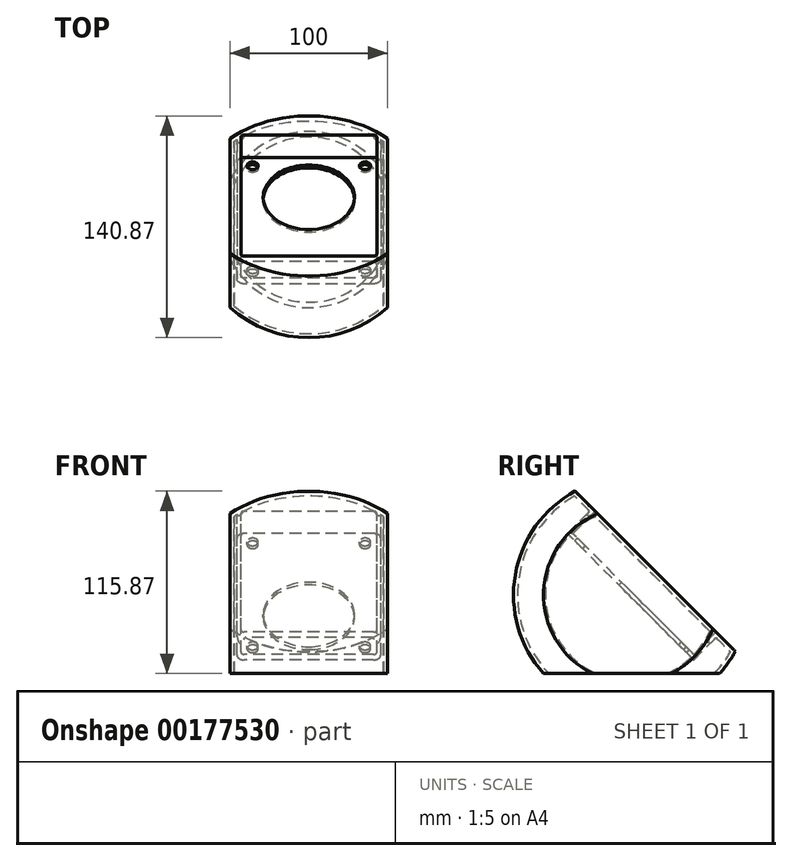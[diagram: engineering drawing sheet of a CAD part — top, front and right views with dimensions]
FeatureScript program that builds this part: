
annotation { "Feature Type Name" : "Feature", "Feature Type Description" : "" }
export const myFeature = defineFeature(function(context is Context, id is Id, definition is map)
    precondition{}
    {
        {
            var Q0;
            Q0=qCreatedBy(makeId("Front.planeOp"),FACE);
            var sketch = newSketch(context, id + "F0", { "sketchPlane" : qUnion([Q0])});
            skArc(sketch, "E0", {"start": v(55.9, 0) * mm, "mid": v(68.47, 80.62) * mm, "end": v(0, 125) * mm});
            skLineSegment(sketch, "E1", {"start": v(0, 0) * mm, "end": v(55.9, 0) * mm});
            skLineSegment(sketch, "E2", {"start": v(0, 50) * mm, "end": v(0, 0) * mm, "construction": true});
            skLineSegment(sketch, "E3", {"start": v(0, 0) * mm, "end": v(0, 125) * mm});
            skPoint(sketch, "E4.orphan", {"position": v(-55.9, 0) * mm});
            skSolve(sketch);
        }
        {
            var Q0;
            Q0=makeQuery(id+"F0.imprint","IMPRINT",FACE,{"disambiguationData":[TD([[makeQuery(id+"F0.imprint","IMPRINT",EDGE,{"derivedFrom":sQuery(id+"F0.wireOp",EDGE,"E0")}),1.0]])]});
            var Q1;
            Q1=sQuery(id+"F0.wireOp",EDGE,"E2");
            revolve(context, id + "F1", {"entities" : qUnion([Q0]), "axis" : qUnion([Q1]), "revolveType" : RevolveType.FULL});
        }
        {
            var Q0;
            Q0=makeQuery(id+"F1.opRevolve","SWEPT_FACE",FACE,{"disambiguationData":[OSD([sQuery(id+"F0.wireOp",EDGE,"E1")])]});
            var sketch = newSketch(context, id + "F2", { "sketchPlane" : qUnion([Q0])});
            skLineSegment(sketch, "E5", {"start": v(74.71, -80) * mm, "end": v(-64.99, -80) * mm, "construction": true});
            skSolve(sketch);
        }
        {
            var Q0;
            Q0=sQuery(id+"F2.wireOp",EDGE,"E5");
            cPlane(context, id + "F3", {"entities" : qUnion([Q0]), "cplaneType" : CPlaneType.LINE_ANGLE, "offset" : 25 * mm, "angle" : 45 * degree, "oppositeDirection" : true, "width" : 150 * mm, "height" : 150 * mm});
        }
        {
            var Q0;
            Q0=qCreatedBy(id+"F3.planeOp",FACE);
            var sketch = newSketch(context, id + "F4", { "sketchPlane" : qUnion([Q0])});
            skLineSegment(sketch, "E6.bottom", {"start": v(-80.9, 121.62) * mm, "end": v(80.9, 121.62) * mm});
            skLineSegment(sketch, "E6.top", {"start": v(-80.9, -121.62) * mm, "end": v(80.9, -121.62) * mm});
            skLineSegment(sketch, "E6.left", {"start": v(-80.9, 121.62) * mm, "end": v(-80.9, -121.62) * mm});
            skLineSegment(sketch, "E6.right", {"start": v(80.9, 121.62) * mm, "end": v(80.9, -121.62) * mm});
            skPoint(sketch, "E6.middle", {"position": v(0, 0) * mm});
            skSolve(sketch);
        }
        {
            var Q0;
            Q0=makeQuery(id+"F4.imprint","IMPRINT",FACE,{"disambiguationData":[TD([[makeQuery(id+"F4.imprint","IMPRINT",EDGE,{"derivedFrom":sQuery(id+"F4.wireOp",EDGE,"E6.bottom")}),-1.0]])]});
            extrude(context, id + "F5", {"entities" : qUnion([Q0]), "operationType" : NewBodyOperationType.REMOVE, "oppositeDirection" : true, "depth" : 100 * mm});
        }
        {
            var Q0;
            Q0=qCreatedBy(id+"F3.planeOp",FACE);
            var sketch = newSketch(context, id + "F6", { "sketchPlane" : qUnion([Q0])});
            skLineSegment(sketch, "E7.bottom", {"start": v(43.2, -17.25) * mm, "end": v(43.2, 87.25) * mm});
            skLineSegment(sketch, "E7.top", {"start": v(-43.2, -17.25) * mm, "end": v(-43.2, 87.25) * mm});
            skLineSegment(sketch, "E7.left", {"start": v(41.2, -19.25) * mm, "end": v(-41.2, -19.25) * mm});
            skLineSegment(sketch, "E7.right", {"start": v(41.2, 89.25) * mm, "end": v(-41.2, 89.25) * mm});
            skPoint(sketch, "E7.middle", {"position": v(0, 35) * mm});
            skPoint(sketch, "E8.visualSharp", {"position": v(-43.2, 89.25) * mm});
            skArc(sketch, "E8.filletArc", {"start": v(-41.2, 89.25) * mm, "mid": v(-42.61, 88.66) * mm, "end": v(-43.2, 87.25) * mm});
            skPoint(sketch, "E9.visualSharp", {"position": v(43.2, 89.25) * mm});
            skArc(sketch, "E9.filletArc", {"start": v(43.2, 87.25) * mm, "mid": v(42.61, 88.66) * mm, "end": v(41.2, 89.25) * mm});
            skPoint(sketch, "E10.visualSharp", {"position": v(43.2, -19.25) * mm});
            skArc(sketch, "E10.filletArc", {"start": v(41.2, -19.25) * mm, "mid": v(42.61, -18.66) * mm, "end": v(43.2, -17.25) * mm});
            skPoint(sketch, "E11.visualSharp", {"position": v(-43.2, -19.25) * mm});
            skArc(sketch, "E11.filletArc", {"start": v(-43.2, -17.25) * mm, "mid": v(-42.61, -18.66) * mm, "end": v(-41.2, -19.25) * mm});
            skCircle(sketch, "E12", {"center": v(0, 16.55) * mm, "radius": 29 * mm});
            skCircle(sketch, "E13", {"center": v(-35.7, 81.75) * mm, "radius": 3.5 * mm});
            skCircle(sketch, "E14", {"center": v(35.7, 81.75) * mm, "radius": 3.5 * mm});
            skCircle(sketch, "E15", {"center": v(35.7, -11.75) * mm, "radius": 3.5 * mm});
            skCircle(sketch, "E16", {"center": v(-35.7, -11.75) * mm, "radius": 3.5 * mm});
            skSolve(sketch);
        }
        {
            var Q0;
            Q0=makeQuery(id+"F6.imprint","IMPRINT",FACE,{"disambiguationData":[TD([[makeQuery(id+"F6.imprint","IMPRINT",EDGE,{"derivedFrom":sQuery(id+"F6.wireOp",EDGE,"E12")}),1.0]])]});
            var Q1;
            Q1=makeQuery(id+"F6.imprint","IMPRINT",FACE,{"disambiguationData":[TD([[makeQuery(id+"F6.imprint","IMPRINT",EDGE,{"derivedFrom":sQuery(id+"F6.wireOp",EDGE,"E13")}),1.0]])]});
            var Q2;
            Q2=makeQuery(id+"F6.imprint","IMPRINT",FACE,{"disambiguationData":[TD([[makeQuery(id+"F6.imprint","IMPRINT",EDGE,{"derivedFrom":sQuery(id+"F6.wireOp",EDGE,"E7.bottom")}),1.0]])]});
            var Q3;
            Q3=makeQuery(id+"F6.imprint","IMPRINT",FACE,{"disambiguationData":[TD([[makeQuery(id+"F6.imprint","IMPRINT",EDGE,{"derivedFrom":sQuery(id+"F6.wireOp",EDGE,"E14")}),1.0]])]});
            var Q4;
            Q4=makeQuery(id+"F6.imprint","IMPRINT",FACE,{"disambiguationData":[TD([[makeQuery(id+"F6.imprint","IMPRINT",EDGE,{"derivedFrom":sQuery(id+"F6.wireOp",EDGE,"E15")}),1.0]])]});
            var Q5;
            Q5=makeQuery(id+"F6.imprint","IMPRINT",FACE,{"disambiguationData":[TD([[makeQuery(id+"F6.imprint","IMPRINT",EDGE,{"derivedFrom":sQuery(id+"F6.wireOp",EDGE,"E16")}),1.0]])]});
            extrude(context, id + "F7", {"entities" : qUnion([Q0, Q1, Q2, Q3, Q4, Q5]), "operationType" : NewBodyOperationType.REMOVE, "depth" : 20 * mm});
        }
        {
            var Q0;
            Q0=qCreatedBy(makeId("Right.planeOp"),FACE);
            cPlane(context, id + "F8", {"entities" : qUnion([Q0]), "cplaneType" : CPlaneType.OFFSET, "offset" : 50 * mm, "width" : 150 * mm, "height" : 150 * mm});
        }
        {
            var Q0;
            Q0=qCreatedBy(makeId("Right.planeOp"),FACE);
            cPlane(context, id + "F9", {"entities" : qUnion([Q0]), "cplaneType" : CPlaneType.OFFSET, "offset" : 50 * mm, "oppositeDirection" : true, "width" : 150 * mm, "height" : 150 * mm});
        }
        {
            var Q0;
            Q0=qCreatedBy(id+"F8.planeOp",FACE);
            var sketch = newSketch(context, id + "F10", { "sketchPlane" : qUnion([Q0])});
            skLineSegment(sketch, "E17.bottom", {"start": v(101.52, 137.25) * mm, "end": v(-101.52, 137.25) * mm});
            skLineSegment(sketch, "E17.top", {"start": v(101.52, -137.25) * mm, "end": v(-101.52, -137.25) * mm});
            skLineSegment(sketch, "E17.left", {"start": v(101.52, 137.25) * mm, "end": v(101.52, -137.25) * mm});
            skLineSegment(sketch, "E17.right", {"start": v(-101.52, 137.25) * mm, "end": v(-101.52, -137.25) * mm});
            skPoint(sketch, "E17.middle", {"position": v(0, 0) * mm});
            skSolve(sketch);
        }
        {
            var Q0;
            Q0=makeQuery(id+"F10.imprint","IMPRINT",FACE,{"disambiguationData":[TD([[makeQuery(id+"F10.imprint","IMPRINT",EDGE,{"derivedFrom":sQuery(id+"F10.wireOp",EDGE,"E17.bottom")}),1.0]])]});
            extrude(context, id + "F11", {"entities" : qUnion([Q0]), "operationType" : NewBodyOperationType.REMOVE, "depth" : 25 * mm});
        }
        {
            var Q0;
            Q0=qCreatedBy(id+"F9.planeOp",FACE);
            var sketch = newSketch(context, id + "F12", { "sketchPlane" : qUnion([Q0])});
            skLineSegment(sketch, "E18.bottom", {"start": v(-88.96, 139.88) * mm, "end": v(88.96, 139.88) * mm});
            skLineSegment(sketch, "E18.top", {"start": v(-88.96, -139.88) * mm, "end": v(88.96, -139.88) * mm});
            skLineSegment(sketch, "E18.left", {"start": v(-88.96, 139.88) * mm, "end": v(-88.96, -139.88) * mm});
            skLineSegment(sketch, "E18.right", {"start": v(88.96, 139.88) * mm, "end": v(88.96, -139.88) * mm});
            skPoint(sketch, "E18.middle", {"position": v(0, 0) * mm});
            skSolve(sketch);
        }
        {
            var Q0;
            Q0=makeQuery(id+"F12.imprint","IMPRINT",FACE,{"disambiguationData":[TD([[makeQuery(id+"F12.imprint","IMPRINT",EDGE,{"derivedFrom":sQuery(id+"F12.wireOp",EDGE,"E18.bottom")}),-1.0]])]});
            extrude(context, id + "F13", {"entities" : qUnion([Q0]), "operationType" : NewBodyOperationType.REMOVE, "oppositeDirection" : true, "depth" : 25 * mm});
        }
        {
            var Q0;
            Q0=makeQuery(id+"F1.opRevolve","SWEPT_FACE",FACE,{"disambiguationData":[OSD([sQuery(id+"F0.wireOp",EDGE,"E1")])]});
            shell(context, id + "F14", {"entities" : qUnion([Q0]), "thickness" : 2.5 * mm});
        }
        {
            var Q0;
            Q0=makeQuery(id+"F6.imprint","IMPRINT",FACE,{"disambiguationData":[TD([[makeQuery(id+"F6.imprint","IMPRINT",EDGE,{"derivedFrom":sQuery(id+"F6.wireOp",EDGE,"E12")}),1.0]])]});
            var Q1;
            Q1=makeQuery(id+"F6.imprint","IMPRINT",FACE,{"disambiguationData":[TD([[makeQuery(id+"F6.imprint","IMPRINT",EDGE,{"derivedFrom":sQuery(id+"F6.wireOp",EDGE,"E14")}),1.0]])]});
            var Q2;
            Q2=makeQuery(id+"F6.imprint","IMPRINT",FACE,{"disambiguationData":[TD([[makeQuery(id+"F6.imprint","IMPRINT",EDGE,{"derivedFrom":sQuery(id+"F6.wireOp",EDGE,"E13")}),1.0]])]});
            var Q3;
            Q3=makeQuery(id+"F6.imprint","IMPRINT",FACE,{"disambiguationData":[TD([[makeQuery(id+"F6.imprint","IMPRINT",EDGE,{"derivedFrom":sQuery(id+"F6.wireOp",EDGE,"E16")}),1.0]])]});
            var Q4;
            Q4=makeQuery(id+"F6.imprint","IMPRINT",FACE,{"disambiguationData":[TD([[makeQuery(id+"F6.imprint","IMPRINT",EDGE,{"derivedFrom":sQuery(id+"F6.wireOp",EDGE,"E15")}),1.0]])]});
            extrude(context, id + "F15", {"entities" : qUnion([Q0, Q1, Q2, Q3, Q4]), "operationType" : NewBodyOperationType.REMOVE, "depth" : 40 * mm});
        }
    });
